# Revit family: VT.COMBI
name_source: partatom
category: Оборудование
units: mm (PartAtom-declared; Revit-internal decimal feet)

## family parameters
Всегда вертикально = Да
Заголовок OmniClass = Climate Control (HVAC)
На основе рабочей плоскости = Нет
Номер OmniClass = 23.75.00.00
Общий = Нет
При загрузке вырезать с полостями = Нет
Размер круглого соединителя = Использовать диаметр
Тип детали = Нормальный
Точка расчета площади = Нет

## types (1)
- VT.COMBI
    BIM главная категория объекта = Водопровод
    BIM категория объекта = Дополнительный
    BIM код категории объекта = Водопровод-дополнительный
    BIM код основной категории объекта = Водопровод
    EMCS Version = 3.0
    Family Version = Rev.00
    IFC классификация = Клапан
    Manufacturer URL = https://valtec.ru
    Revit Version = 2018
    URL = https://valtec.ru
    URL бренда = https://valtec.ru
    URL продукта = https://valtec.ru
    Uniclass 1.4 Описание = Арматура
    Uniclass 2.0 Описание = Арматура
    Uniclass 2015 Имя = Системы отопления, охлаждения и охлаждения
    Uniformat II Description = HVAC
    Вес нетто (Kg) = 0
    Гидравлический возвратный поток = 0.0 л/с
    Гидравлический поток подачи = 0.0 л/с
    Группа модели = COMBI/S
    Группа товаров = Смесительно группа для систем COMBIMIX
    Изготовитель = IVAR
    Инструкции по установке = https://valtec.ru
    Линия продуктов = радиаторные системы
    Макс рабочая температура = 100 °C
    Макс рабочее давление = 1000000.0 Па
    Мастерформат 2014 Описание = Отопление, вентиляция и кондиционирование воздуха (HVAC)
    Материал вторичный = Copper
    Материал основной = Brass
    Название производителя = IVAR
    Номинальная высота = 0 мм
    Номинальная ширина = 0 мм
    Общий поток подачи гидравлики = 0.0 л/с
    Описание = Насосно-смесительный узел
    Описание NBS = Арматура
    Описание OmniClass = Арматура
    Описание Конфигурации = Регулятор COMBIMIX для излучающих систем.
    Описание статьи = Насосно-смесительный узел
    Полный гидравлический возвратный поток = 0.0 л/с
    Практическое руководство по использованию семьи = - Вы должны выбрать тип смешивания. Отметьте эту опцию в параметрах «Свойства модели - смешивание с фиксированной точкой» или «Свойства модели - смешивание с внешней компенсированной температурой».
- Вы должны выбрать место для насоса. Отметьте этот параметр в параметрах «Свойства модели - 130 мм пространства насоса» или «Свойства модели - 180 мм пространства насоса».
- Вы должны выбрать, если насос включен или нет. Установите этот флажок в параметрах «Свойства модели - насос включен» или «Свойства модели - насос не включен».
- Вы должны выбрать версию без байпаса (ожидается электронный насос с переменной скоростью) или с байпасом (ожидается стандартный трехскоростной насос). Отметьте эту опцию в параметрах «Свойства модели - байпас для электронасоса с переменной скоростью» или «Свойства модели - байпас для трехскоростного насоса».
    Продукт = COMBIMIX
    Произведено в = Сделано в Италии
    Размер соединения = G 1"
    Размеры соединения насоса = G 1"1/2F flat seal
    Семейство продуктов = Насосно-смесительный узел
    Страна производитель = Italy
    Техническое описание = https://valtec.ru
    Тип статьи = COMBI/S
